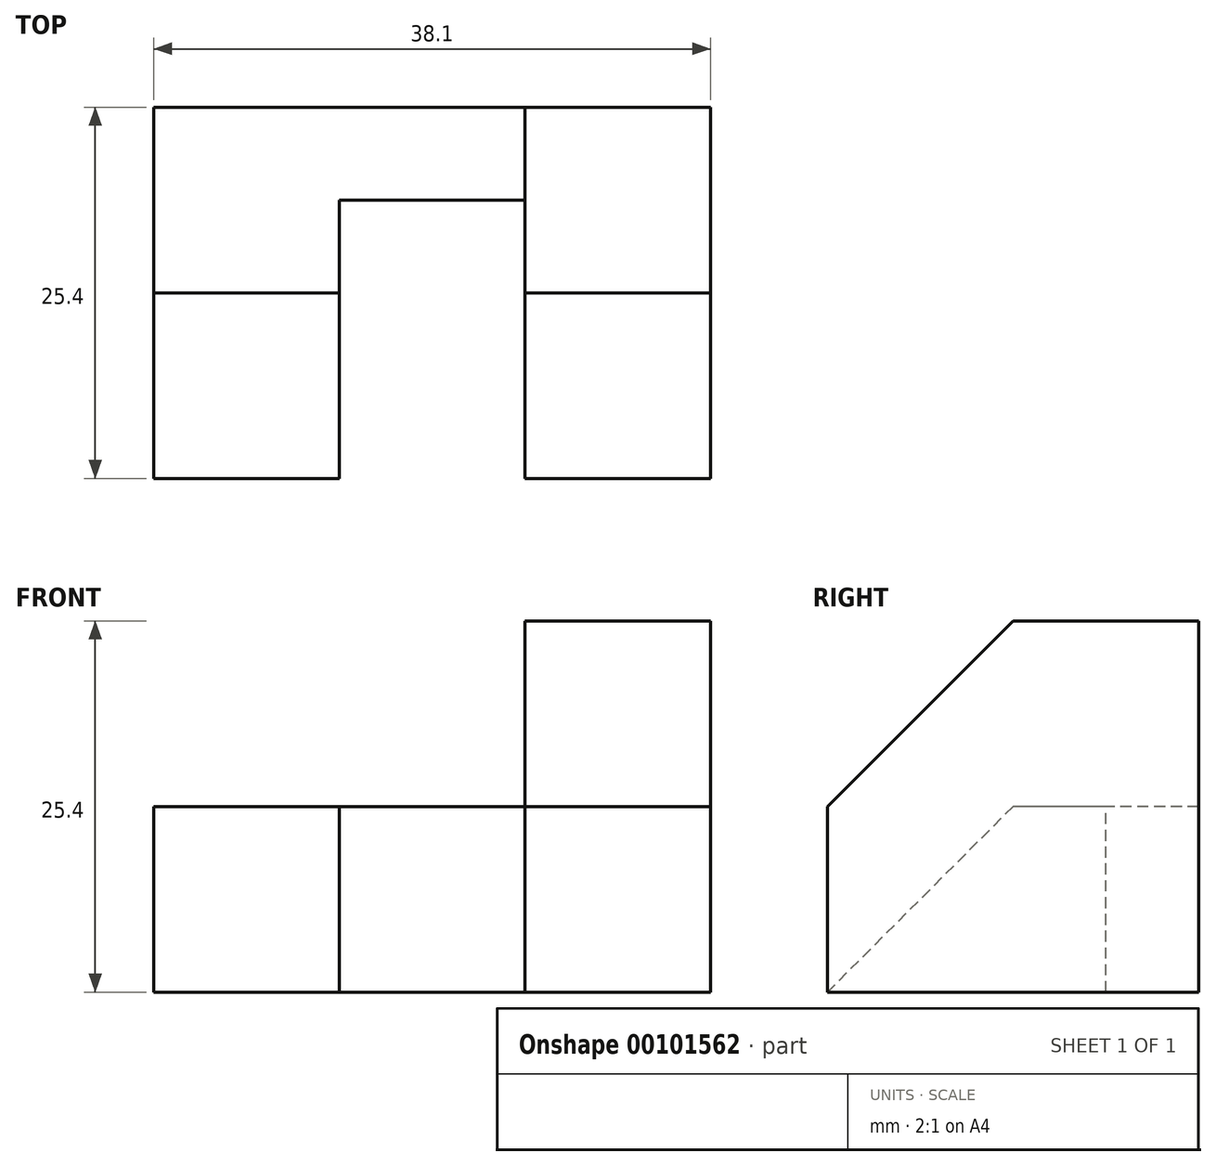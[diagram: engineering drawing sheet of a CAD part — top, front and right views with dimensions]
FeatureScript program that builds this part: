
annotation { "Feature Type Name" : "Feature", "Feature Type Description" : "" }
export const myFeature = defineFeature(function(context is Context, id is Id, definition is map)
    precondition{}
    {
        {
            var Q0;
            Q0=qCreatedBy(makeId("Right.planeOp"),FACE);
            var sketch = newSketch(context, id + "F0", { "sketchPlane" : qUnion([Q0])});
            skLineSegment(sketch, "E0", {"start": v(0, 0) * mm, "end": v(25.4, 0) * mm});
            skLineSegment(sketch, "E1", {"start": v(25.4, 0) * mm, "end": v(25.4, 25.4) * mm});
            skLineSegment(sketch, "E2", {"start": v(25.4, 25.4) * mm, "end": v(12.7, 25.4) * mm});
            skLineSegment(sketch, "E3", {"start": v(12.7, 25.4) * mm, "end": v(0, 12.7) * mm});
            skLineSegment(sketch, "E4", {"start": v(0, 12.7) * mm, "end": v(0, 0) * mm});
            skSolve(sketch);
        }
        {
            var Q0;
            Q0=makeQuery(id+"F0.imprint","IMPRINT",FACE,{"disambiguationData":[TD([[makeQuery(id+"F0.imprint","IMPRINT",EDGE,{"derivedFrom":sQuery(id+"F0.wireOp",EDGE,"E0")}),1.0]])]});
            extrude(context, id + "F1", {"entities" : qUnion([Q0]), "depth" : 12.7 * mm});
        }
        {
            var Q0;
            Q0=qCreatedBy(makeId("Right.planeOp"),FACE);
            var sketch = newSketch(context, id + "F2", { "sketchPlane" : qUnion([Q0])});
            skLineSegment(sketch, "E5", {"start": v(0, 0) * mm, "end": v(25.4, 0) * mm});
            skLineSegment(sketch, "E6", {"start": v(25.4, 0) * mm, "end": v(25.4, 12.7) * mm});
            skLineSegment(sketch, "E7", {"start": v(25.4, 12.7) * mm, "end": v(12.7, 12.7) * mm});
            skLineSegment(sketch, "E8", {"start": v(12.7, 12.7) * mm, "end": v(0, 0) * mm});
            skSolve(sketch);
        }
        {
            var Q0;
            Q0 = qSketchRegion(id + "F2", true);
            extrude(context, id + "F3", {"entities" : qUnion([Q0]), "oppositeDirection" : true, "depth" : 25.4 * mm});
        }
        {
            var Q0;
            Q0=qCreatedBy(makeId("Right.planeOp"),FACE);
            var sketch = newSketch(context, id + "F4", { "sketchPlane" : qUnion([Q0])});
            skLineSegment(sketch, "E9", {"start": v(0, 0) * mm, "end": v(19.05, 0) * mm});
            skLineSegment(sketch, "E10", {"start": v(19.05, 0) * mm, "end": v(19.05, 12.7) * mm});
            skLineSegment(sketch, "E11", {"start": v(19.05, 12.7) * mm, "end": v(12.7, 12.7) * mm});
            skLineSegment(sketch, "E12", {"start": v(12.7, 12.7) * mm, "end": v(0, 0) * mm});
            skSolve(sketch);
        }
        {
            var Q0;
            Q0 = qSketchRegion(id + "F4", true);
            extrude(context, id + "F5", {"entities" : qUnion([Q0]), "operationType" : NewBodyOperationType.REMOVE, "oppositeDirection" : true, "depth" : 12.7 * mm});
        }
    });
